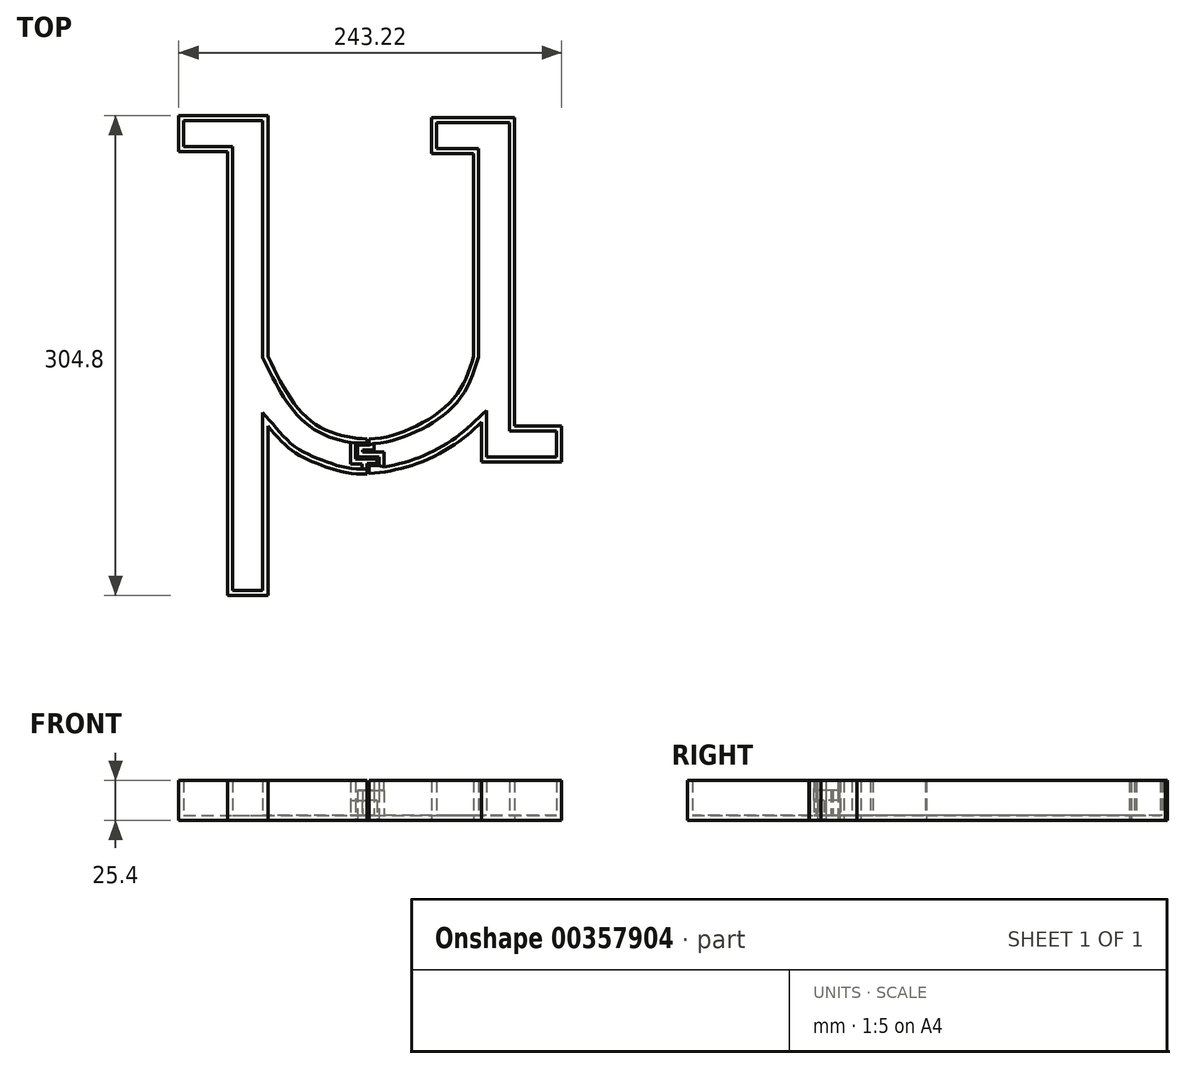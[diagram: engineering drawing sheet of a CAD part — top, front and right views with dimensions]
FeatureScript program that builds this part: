
annotation { "Feature Type Name" : "Feature", "Feature Type Description" : "" }
export const myFeature = defineFeature(function(context is Context, id is Id, definition is map)
    precondition{}
    {
        {
            var Q0;
            Q0=qCreatedBy(makeId("Top.planeOp"),FACE);
            var sketch = newSketch(context, id + "F0", { "sketchPlane" : qUnion([Q0])});
            skLineSegment(sketch, "E0", {"start": v(78.61, 172.3) * mm, "end": v(135.22, 172.3) * mm});
            skLineSegment(sketch, "E1", {"start": v(135.22, 172.3) * mm, "end": v(135.22, 19.28) * mm});
            skLineSegment(sketch, "E2", {"start": v(78.61, 172.3) * mm, "end": v(78.61, 149.29) * mm});
            skLineSegment(sketch, "E3", {"start": v(78.61, 149.29) * mm, "end": v(109.71, 149.29) * mm});
            skLineSegment(sketch, "E4", {"start": v(109.71, 149.29) * mm, "end": v(109.71, -132.5) * mm});
            skLineSegment(sketch, "E5", {"start": v(109.71, -132.5) * mm, "end": v(135.22, -132.5) * mm});
            skLineSegment(sketch, "E6", {"start": v(135.22, -132.5) * mm, "end": v(135.22, -24.88) * mm});
            skFitSpline(sketch, "E7", {"points": [v(135.22, 19.28) * mm, v(162.59, -21.77) * mm, v(195.56, -32.97) * mm, v(217.33, -29.86) * mm, v(242.2, -17.42) * mm, v(258.38, 0) * mm, v(265.85, 19.28) * mm], "startDerivative": vector(107.11, -219.88) * mm, "endDerivative": vector(42.3, 140.77) * mm});
            skLineSegment(sketch, "E8", {"start": v(265.85, 19.28) * mm, "end": v(265.85, 148.05) * mm});
            skLineSegment(sketch, "E9", {"start": v(265.85, 148.05) * mm, "end": v(239.1, 148.05) * mm});
            skLineSegment(sketch, "E10", {"start": v(239.1, 148.05) * mm, "end": v(239.1, 171.06) * mm});
            skLineSegment(sketch, "E11", {"start": v(239.1, 171.06) * mm, "end": v(291.97, 171.06) * mm});
            skLineSegment(sketch, "E12", {"start": v(291.97, 171.06) * mm, "end": v(291.97, -24.88) * mm});
            skLineSegment(sketch, "E13", {"start": v(291.97, -24.88) * mm, "end": v(321.83, -24.88) * mm});
            skLineSegment(sketch, "E14", {"start": v(321.83, -24.88) * mm, "end": v(321.83, -47.9) * mm});
            skLineSegment(sketch, "E15", {"start": v(321.83, -47.9) * mm, "end": v(270.82, -47.9) * mm});
            skLineSegment(sketch, "E16", {"start": v(270.82, -47.9) * mm, "end": v(270.82, -22.4) * mm});
            skPoint(sketch, "E17.2.internal.snap0", {"position": v(296.33, -47.9) * mm});
            skPoint(sketch, "E17.5.internal.snap0", {"position": v(296.33, -47.9) * mm});
            skFitSpline(sketch, "E17", {"points": [v(270.82, -22.4) * mm, v(256.52, -34.83) * mm, v(232.26, -47.9) * mm, v(208.62, -54.12) * mm, v(186.23, -54.74) * mm, v(164.45, -47.9) * mm, v(149.52, -39.81) * mm, v(135.22, -24.88) * mm], "startDerivative": vector(-97.2, -94.17) * mm, "endDerivative": vector(-100.63, 119.1) * mm});
            skSolve(sketch);
        }
        {
            var Q0;
            Q0=makeQuery(id+"F0.imprint","IMPRINT",FACE,{"disambiguationData":[TD([[makeQuery(id+"F0.imprint","IMPRINT",EDGE,{"derivedFrom":sQuery(id+"F0.wireOp",EDGE,"E0")}),-1.0]])]});
            extrude(context, id + "F1", {"entities" : qUnion([Q0]), "depth" : 25.4 * mm});
        }
        {
            var Q0;
            Q0=makeQuery(id+"F1.opExtrude","CAP_FACE",FACE,{"disambiguationData":[OSD([sQuery(id+"F0.wireOp",EDGE,"E0"),sQuery(id+"F0.wireOp",EDGE,"E1"),sQuery(id+"F0.wireOp",EDGE,"E2"),sQuery(id+"F0.wireOp",EDGE,"E3"),sQuery(id+"F0.wireOp",EDGE,"E4"),sQuery(id+"F0.wireOp",EDGE,"E5"),sQuery(id+"F0.wireOp",EDGE,"E6"),sQuery(id+"F0.wireOp",EDGE,"E7"),sQuery(id+"F0.wireOp",EDGE,"E8"),sQuery(id+"F0.wireOp",EDGE,"E9"),sQuery(id+"F0.wireOp",EDGE,"E10"),sQuery(id+"F0.wireOp",EDGE,"E11"),sQuery(id+"F0.wireOp",EDGE,"E12"),sQuery(id+"F0.wireOp",EDGE,"E13"),sQuery(id+"F0.wireOp",EDGE,"E14"),sQuery(id+"F0.wireOp",EDGE,"E15"),sQuery(id+"F0.wireOp",EDGE,"E16"),sQuery(id+"F0.wireOp",EDGE,"E17")])],"isStart":true});
            var sketch = newSketch(context, id + "F2", { "sketchPlane" : qUnion([Q0])});
            skLineSegment(sketch, "E18", {"start": v(199.46, 33.05) * mm, "end": v(199.46, 36.93) * mm});
            skLineSegment(sketch, "E19", {"start": v(199.46, 36.93) * mm, "end": v(192.3, 36.93) * mm});
            skLineSegment(sketch, "E20", {"start": v(192.3, 36.93) * mm, "end": v(192.3, 44.66) * mm});
            skLineSegment(sketch, "E21", {"start": v(192.3, 44.66) * mm, "end": v(199.46, 44.66) * mm});
            skLineSegment(sketch, "E22", {"start": v(199.46, 44.66) * mm, "end": v(205.94, 44.66) * mm});
            skLineSegment(sketch, "E23", {"start": v(205.94, 44.66) * mm, "end": v(205.94, 50.09) * mm});
            skLineSegment(sketch, "E24", {"start": v(205.94, 50.09) * mm, "end": v(199.46, 50.09) * mm});
            skLineSegment(sketch, "E25.trimOffspring", {"start": v(199.46, 50.09) * mm, "end": v(199.46, 55.2) * mm});
            skLineSegment(sketch, "E26", {"start": v(199.46, 33.05) * mm, "end": v(199.46, 25.9) * mm});
            skLineSegment(sketch, "E27", {"start": v(199.46, 55.2) * mm, "end": v(199.46, 61.93) * mm});
            skLineSegment(sketch, "E28.0", {"start": v(198.2, 33.05) * mm, "end": v(198.2, 25.9) * mm});
            skLineSegment(sketch, "E28.1", {"start": v(198.2, 33.05) * mm, "end": v(198.2, 35.66) * mm});
            skLineSegment(sketch, "E28.2", {"start": v(198.2, 35.66) * mm, "end": v(191.02, 35.66) * mm});
            skLineSegment(sketch, "E28.3", {"start": v(191.02, 35.66) * mm, "end": v(191.02, 45.93) * mm});
            skLineSegment(sketch, "E28.4", {"start": v(191.02, 45.93) * mm, "end": v(199.46, 45.93) * mm});
            skLineSegment(sketch, "E28.5", {"start": v(199.46, 45.93) * mm, "end": v(204.67, 45.93) * mm});
            skLineSegment(sketch, "E28.6", {"start": v(198.2, 55.2) * mm, "end": v(198.2, 61.93) * mm});
            skLineSegment(sketch, "E28.7", {"start": v(198.2, 48.82) * mm, "end": v(198.2, 55.2) * mm});
            skLineSegment(sketch, "E28.8", {"start": v(204.67, 48.82) * mm, "end": v(198.2, 48.82) * mm});
            skLineSegment(sketch, "E28.9", {"start": v(204.67, 45.93) * mm, "end": v(204.67, 48.82) * mm});
            skLineSegment(sketch, "E29", {"start": v(199.46, 25.9) * mm, "end": v(198.2, 25.9) * mm});
            skLineSegment(sketch, "E30", {"start": v(199.46, 61.93) * mm, "end": v(198.2, 61.93) * mm});
            skSolve(sketch);
        }
        {
            var Q0;
            {var subQ1=sQuery(id+"F2.wireOp",EDGE,"E18");Q0=makeQuery(id+"F2.imprint","IMPRINT",FACE,{"disambiguationData":[TD([[makeQuery(id+"F2.imprint","IMPRINT",EDGE,{"derivedFrom":subQ1}),1.0]])]});}
            extrude(context, id + "F3", {"entities" : qUnion([Q0]), "operationType" : NewBodyOperationType.REMOVE, "oppositeDirection" : true, "depth" : 25.4 * mm});
        }
        {
            var Q0;
            {var subQ0=sQuery(id+"F0.wireOp",EDGE,"E7");var subQ1=sQuery(id+"F0.wireOp",EDGE,"E17");var subQ2=sQuery(id+"F0.wireOp",EDGE,"E6");var subQ3=sQuery(id+"F0.wireOp",EDGE,"E5");var subQ4=sQuery(id+"F0.wireOp",EDGE,"E4");var subQ5=sQuery(id+"F0.wireOp",EDGE,"E0");var subQ6=sQuery(id+"F0.wireOp",EDGE,"E3");var subQ7=sQuery(id+"F0.wireOp",EDGE,"E1");var subQ8=sQuery(id+"F0.wireOp",EDGE,"E2");Q0=makeQuery(id+"F3.boolean.opBoolean","SPLIT",FACE,{"disambiguationData":[TD([makeQuery(id+"F1.opExtrude","SWEPT_FACE",FACE,{"disambiguationData":[OSD([subQ5])]})])],"derivedFrom":makeQuery(id+"F1.opExtrude","CAP_FACE",FACE,{"disambiguationData":[OSD([subQ5,subQ7,subQ8,subQ6,subQ4,subQ3,subQ2,subQ0,sQuery(id+"F0.wireOp",EDGE,"E8"),sQuery(id+"F0.wireOp",EDGE,"E9"),sQuery(id+"F0.wireOp",EDGE,"E10"),sQuery(id+"F0.wireOp",EDGE,"E11"),sQuery(id+"F0.wireOp",EDGE,"E12"),sQuery(id+"F0.wireOp",EDGE,"E13"),sQuery(id+"F0.wireOp",EDGE,"E14"),sQuery(id+"F0.wireOp",EDGE,"E15"),sQuery(id+"F0.wireOp",EDGE,"E16"),subQ1])],"isStart":false})});}
            var Q1;
            {var subQ0=sQuery(id+"F0.wireOp",EDGE,"E16");var subQ1=sQuery(id+"F0.wireOp",EDGE,"E15");var subQ2=sQuery(id+"F0.wireOp",EDGE,"E14");var subQ3=sQuery(id+"F0.wireOp",EDGE,"E13");var subQ4=sQuery(id+"F0.wireOp",EDGE,"E12");var subQ5=sQuery(id+"F0.wireOp",EDGE,"E11");var subQ6=sQuery(id+"F0.wireOp",EDGE,"E7");var subQ7=sQuery(id+"F0.wireOp",EDGE,"E8");var subQ8=sQuery(id+"F0.wireOp",EDGE,"E9");var subQ9=sQuery(id+"F0.wireOp",EDGE,"E10");var subQ10=sQuery(id+"F0.wireOp",EDGE,"E17");Q1=makeQuery(id+"F3.boolean.opBoolean","SPLIT",FACE,{"disambiguationData":[TD([makeQuery(id+"F1.opExtrude","SWEPT_FACE",FACE,{"disambiguationData":[OSD([subQ7])]})])],"derivedFrom":makeQuery(id+"F1.opExtrude","CAP_FACE",FACE,{"disambiguationData":[OSD([sQuery(id+"F0.wireOp",EDGE,"E0"),sQuery(id+"F0.wireOp",EDGE,"E1"),sQuery(id+"F0.wireOp",EDGE,"E2"),sQuery(id+"F0.wireOp",EDGE,"E3"),sQuery(id+"F0.wireOp",EDGE,"E4"),sQuery(id+"F0.wireOp",EDGE,"E5"),sQuery(id+"F0.wireOp",EDGE,"E6"),subQ6,subQ7,subQ8,subQ9,subQ5,subQ4,subQ3,subQ2,subQ1,subQ0,subQ10])],"isStart":false})});}
            shell(context, id + "F4", {"entities" : qUnion([Q0, Q1]), "thickness" : 3.17 * mm});
        }
        {
            var Q0;
            {var subQ0=sQuery(id+"F0.wireOp",EDGE,"E7");var subQ1=sQuery(id+"F0.wireOp",EDGE,"E17");var subQ2=sQuery(id+"F0.wireOp",EDGE,"E6");var subQ3=sQuery(id+"F0.wireOp",EDGE,"E5");var subQ4=sQuery(id+"F0.wireOp",EDGE,"E4");var subQ5=sQuery(id+"F0.wireOp",EDGE,"E0");var subQ6=sQuery(id+"F0.wireOp",EDGE,"E3");var subQ7=sQuery(id+"F0.wireOp",EDGE,"E1");var subQ8=sQuery(id+"F0.wireOp",EDGE,"E2");Q0=makeQuery(id+"F3.boolean.opBoolean","SPLIT",FACE,{"disambiguationData":[TD([makeQuery(id+"F1.opExtrude","SWEPT_FACE",FACE,{"disambiguationData":[OSD([subQ5])]})])],"derivedFrom":makeQuery(id+"F1.opExtrude","CAP_FACE",FACE,{"disambiguationData":[OSD([subQ5,subQ7,subQ8,subQ6,subQ4,subQ3,subQ2,subQ0,sQuery(id+"F0.wireOp",EDGE,"E8"),sQuery(id+"F0.wireOp",EDGE,"E9"),sQuery(id+"F0.wireOp",EDGE,"E10"),sQuery(id+"F0.wireOp",EDGE,"E11"),sQuery(id+"F0.wireOp",EDGE,"E12"),sQuery(id+"F0.wireOp",EDGE,"E13"),sQuery(id+"F0.wireOp",EDGE,"E14"),sQuery(id+"F0.wireOp",EDGE,"E15"),sQuery(id+"F0.wireOp",EDGE,"E16"),subQ1])],"isStart":false})});}
            var sketch = newSketch(context, id + "F5", { "sketchPlane" : qUnion([Q0])});
            skLineSegment(sketch, "E31", {"start": v(187.85, -35.35) * mm, "end": v(191.02, -35.66) * mm});
            skLineSegment(sketch, "E32", {"start": v(195.02, -52.18) * mm, "end": v(198.2, -52.18) * mm});
            skSolve(sketch);
        }
        {
            var Q0;
            Q0=makeQuery(id+"F5.imprint","IMPRINT",FACE,{"disambiguationData":[TD([[makeQuery(id+"F5.imprint","IMPRINT",EDGE,{"derivedFrom":sQuery(id+"F5.wireOp",EDGE,"E31")}),-1.0]])]});
            extrude(context, id + "F6", {"entities" : qUnion([Q0]), "operationType" : NewBodyOperationType.REMOVE, "oppositeDirection" : true, "depth" : 12.7 * mm});
        }
        {
            var Q0;
            {var subQ0=sQuery(id+"F0.wireOp",EDGE,"E16");var subQ1=sQuery(id+"F0.wireOp",EDGE,"E15");var subQ2=sQuery(id+"F0.wireOp",EDGE,"E14");var subQ3=sQuery(id+"F0.wireOp",EDGE,"E13");var subQ4=sQuery(id+"F0.wireOp",EDGE,"E12");var subQ5=sQuery(id+"F0.wireOp",EDGE,"E11");var subQ6=sQuery(id+"F0.wireOp",EDGE,"E7");var subQ7=sQuery(id+"F0.wireOp",EDGE,"E8");var subQ8=sQuery(id+"F0.wireOp",EDGE,"E9");var subQ9=sQuery(id+"F0.wireOp",EDGE,"E10");var subQ10=sQuery(id+"F0.wireOp",EDGE,"E17");Q0=makeQuery(id+"F3.boolean.opBoolean","SPLIT",FACE,{"disambiguationData":[TD([makeQuery(id+"F1.opExtrude","SWEPT_FACE",FACE,{"disambiguationData":[OSD([subQ7])]})])],"derivedFrom":makeQuery(id+"F1.opExtrude","CAP_FACE",FACE,{"disambiguationData":[OSD([sQuery(id+"F0.wireOp",EDGE,"E0"),sQuery(id+"F0.wireOp",EDGE,"E1"),sQuery(id+"F0.wireOp",EDGE,"E2"),sQuery(id+"F0.wireOp",EDGE,"E3"),sQuery(id+"F0.wireOp",EDGE,"E4"),sQuery(id+"F0.wireOp",EDGE,"E5"),sQuery(id+"F0.wireOp",EDGE,"E6"),subQ6,subQ7,subQ8,subQ9,subQ5,subQ4,subQ3,subQ2,subQ1,subQ0,subQ10])],"isStart":false})});}
            var sketch = newSketch(context, id + "F7", { "sketchPlane" : qUnion([Q0])});
            skLineSegment(sketch, "E33", {"start": v(209.12, -50.82) * mm, "end": v(205.94, -50.09) * mm});
            skLineSegment(sketch, "E34", {"start": v(199.46, -36.93) * mm, "end": v(202.64, -36.1) * mm});
            skSolve(sketch);
        }
        {
            var Q0;
            Q0=makeQuery(id+"F7.imprint","IMPRINT",FACE,{"disambiguationData":[TD([[makeQuery(id+"F7.imprint","IMPRINT",EDGE,{"derivedFrom":sQuery(id+"F7.wireOp",EDGE,"E33")}),-1.0]])]});
            extrude(context, id + "F8", {"entities" : qUnion([Q0]), "operationType" : NewBodyOperationType.REMOVE, "oppositeDirection" : true, "depth" : 6.35 * mm});
        }
    });
